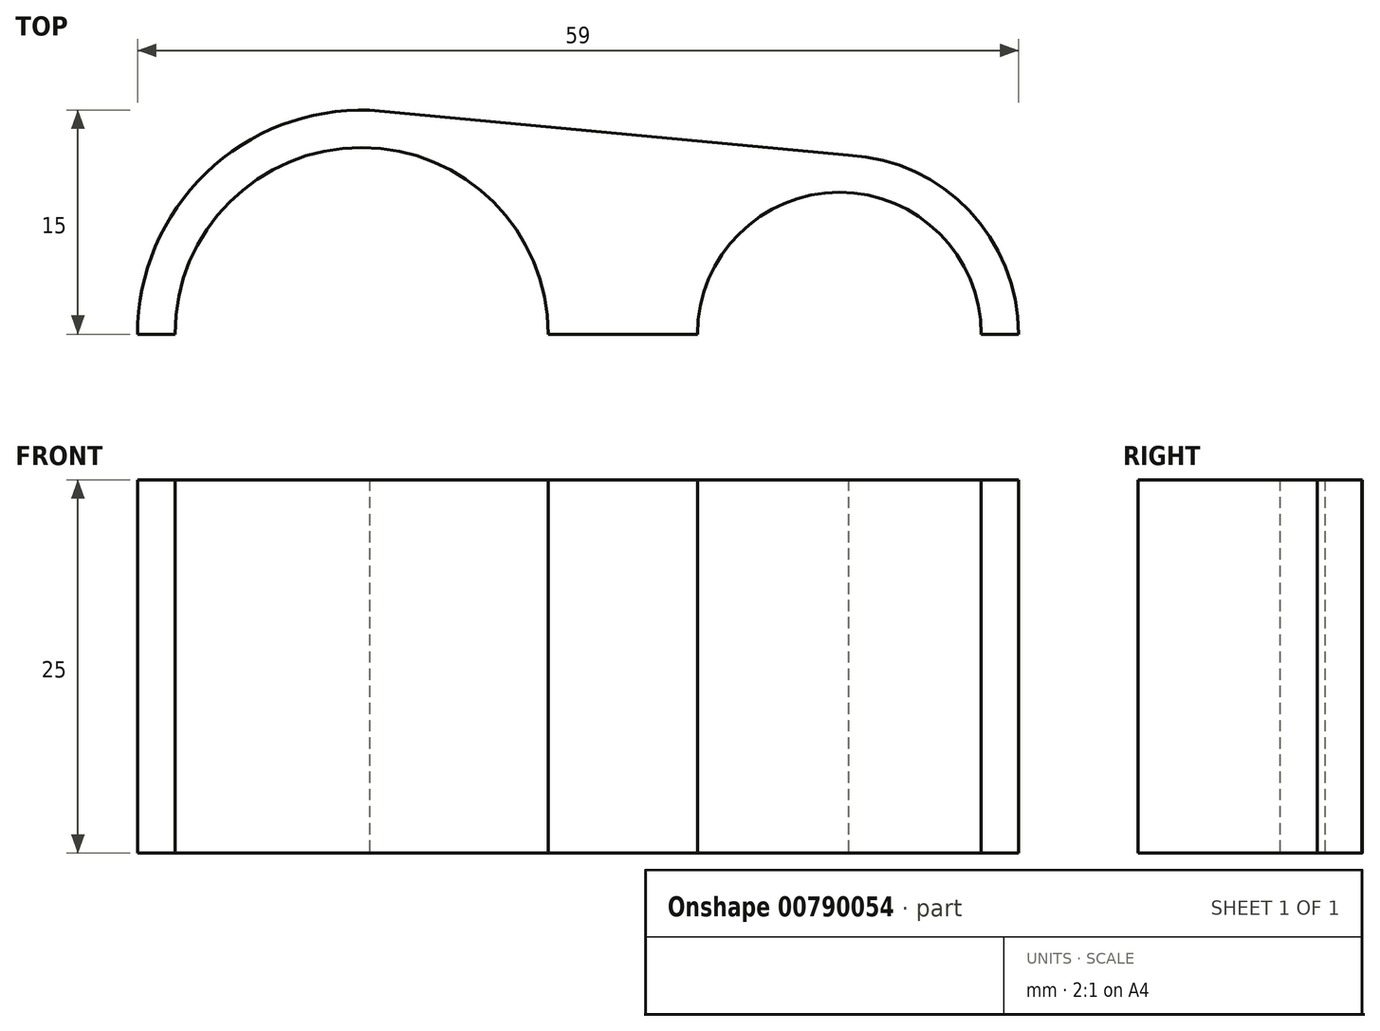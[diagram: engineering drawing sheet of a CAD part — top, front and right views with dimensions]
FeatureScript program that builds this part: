
annotation { "Feature Type Name" : "Feature", "Feature Type Description" : "" }
export const myFeature = defineFeature(function(context is Context, id is Id, definition is map)
    precondition{}
    {
        {
            var Q0;
            Q0=qCreatedBy(makeId("Top.planeOp"),FACE);
            var sketch = newSketch(context, id + "F0", { "sketchPlane" : qUnion([Q0])});
            skArc(sketch, "E0", {"start": v(-15.23, 14.83) * mm, "mid": v(-32.5, -0.43) * mm, "end": v(-14.37, -14.67) * mm});
            skArc(sketch, "E1", {"start": v(14.78, -12) * mm, "mid": v(26.5, -0.16) * mm, "end": v(15.1, 11.98) * mm});
            skLineSegment(sketch, "E2", {"start": v(15.1, 11.98) * mm, "end": v(-16.98, 15) * mm});
            skLineSegment(sketch, "E3", {"start": v(-17.9, -15) * mm, "end": v(14.78, -12) * mm});
            skCircle(sketch, "E4", {"center": v(-17.5, 0) * mm, "radius": 12.5 * mm});
            skCircle(sketch, "E5", {"center": v(14.5, 0) * mm, "radius": 9.5 * mm});
            skSolve(sketch);
        }
        {
            var Q0;
            {var subQ4=sQuery(id+"F0.wireOp",EDGE,"E1");Q0=makeQuery(id+"F0.imprint","IMPRINT",FACE,{"disambiguationData":[TD([[makeQuery(id+"F0.imprint","IMPRINT",EDGE,{"derivedFrom":subQ4}),1.0]])]});}
            extrude(context, id + "F1", {"entities" : qUnion([Q0]), "depth" : 25 * mm, "offsetDistance" : 25 * mm});
        }
        {
            var Q0;
            Q0=qCreatedBy(makeId("Top.planeOp"),FACE);
            var sketch = newSketch(context, id + "F2", { "sketchPlane" : qUnion([Q0])});
            skLineSegment(sketch, "E6.bottom", {"start": v(-36.24, 0) * mm, "end": v(32.6, 0) * mm});
            skLineSegment(sketch, "E6.top", {"start": v(-36.24, -15.53) * mm, "end": v(32.6, -15.53) * mm});
            skLineSegment(sketch, "E6.left", {"start": v(-36.24, 0) * mm, "end": v(-36.24, -15.53) * mm});
            skLineSegment(sketch, "E6.right", {"start": v(32.6, 0) * mm, "end": v(32.6, -15.53) * mm});
            skSolve(sketch);
        }
        {
            var Q0;
            Q0=makeQuery(id+"F2.imprint","IMPRINT",FACE,{"disambiguationData":[TD([[makeQuery(id+"F2.imprint","IMPRINT",EDGE,{"derivedFrom":sQuery(id+"F2.wireOp",EDGE,"E6.bottom")}),-1.0]])]});
            extrude(context, id + "F3", {"entities" : qUnion([Q0]), "operationType" : NewBodyOperationType.REMOVE, "depth" : 25 * mm, "offsetDistance" : 25 * mm});
        }
        {
            var Q0;
            Q0=makeQuery(id+"F1.opExtrude","CAP_FACE",FACE,{"disambiguationData":[OSD([sQuery(id+"F0.wireOp",EDGE,"E0"),sQuery(id+"F0.wireOp",EDGE,"E1"),sQuery(id+"F0.wireOp",EDGE,"E2"),sQuery(id+"F0.wireOp",EDGE,"E3"),sQuery(id+"F0.wireOp",EDGE,"E4"),sQuery(id+"F0.wireOp",EDGE,"E5")])],"isStart":false});
            cPlane(context, id + "F4", {"entities" : qUnion([Q0]), "cplaneType" : CPlaneType.OFFSET, "offset" : 12.5 * mm, "oppositeDirection" : true, "width" : 150 * mm, "height" : 150 * mm});
        }
    });
